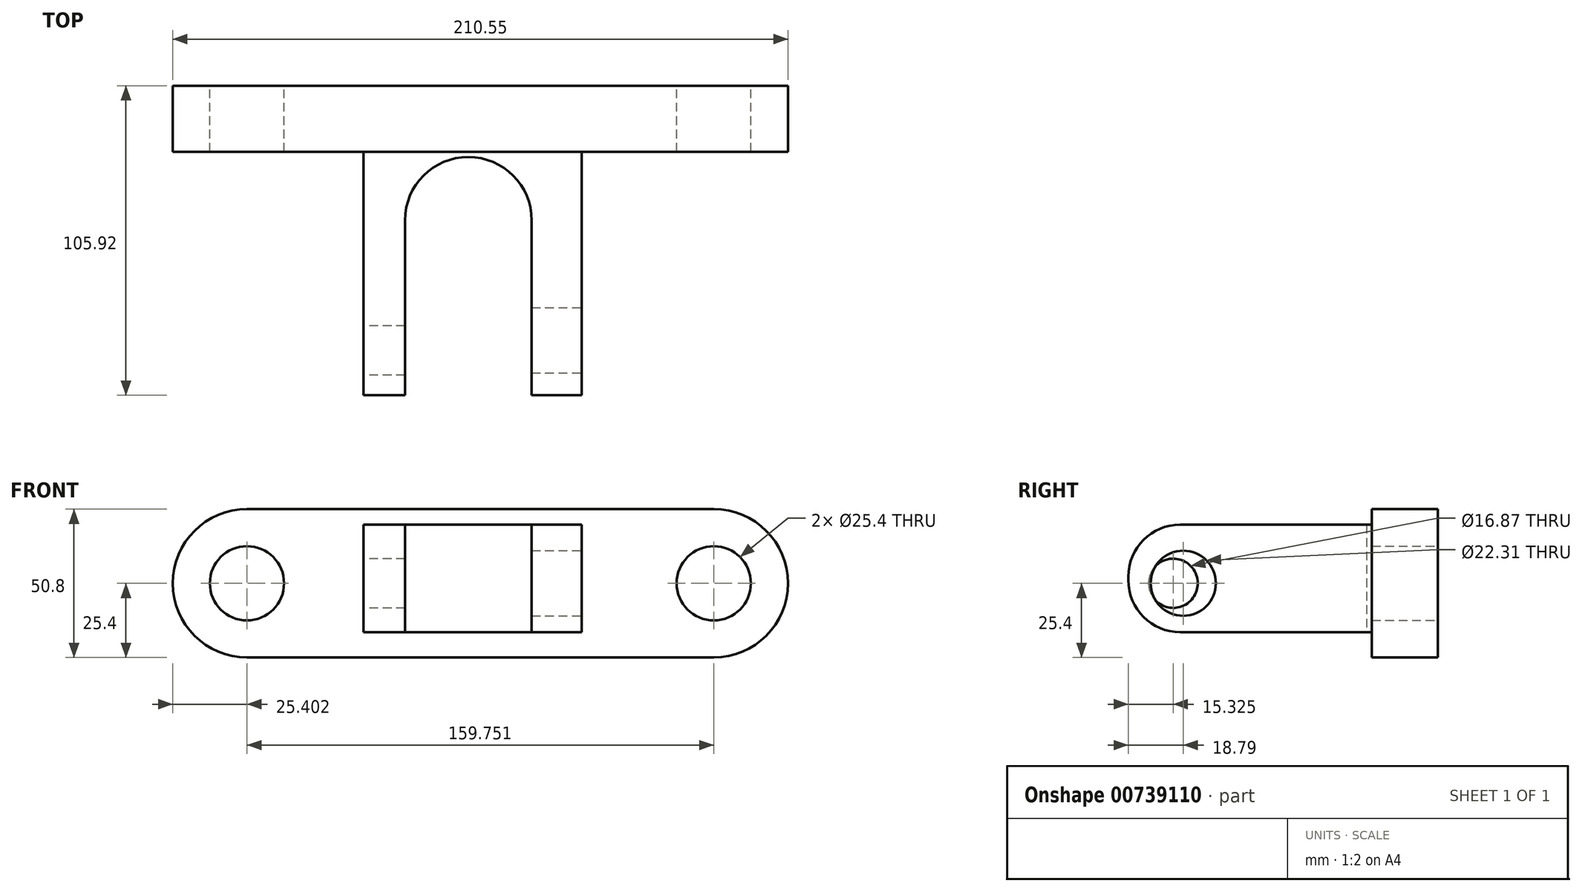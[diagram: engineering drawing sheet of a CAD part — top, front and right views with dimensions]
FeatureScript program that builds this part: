
annotation { "Feature Type Name" : "Feature", "Feature Type Description" : "" }
export const myFeature = defineFeature(function(context is Context, id is Id, definition is map)
    precondition{}
    {
        {
            var Q0;
            Q0=qCreatedBy(makeId("Front.planeOp"),FACE);
            var sketch = newSketch(context, id + "F0", { "sketchPlane" : qUnion([Q0])});
            skArc(sketch, "E0", {"start": v(-77.2, 25.4) * mm, "mid": v(-102.6, 0) * mm, "end": v(-77.2, -25.4) * mm});
            skArc(sketch, "E1", {"start": v(82.55, -25.4) * mm, "mid": v(107.95, 0) * mm, "end": v(82.55, 25.4) * mm});
            skLineSegment(sketch, "E2", {"start": v(-77.2, 25.4) * mm, "end": v(82.55, 25.4) * mm});
            skLineSegment(sketch, "E3", {"start": v(-77.2, -25.4) * mm, "end": v(82.55, -25.4) * mm});
            skCircle(sketch, "E4", {"center": v(-77.2, 0) * mm, "radius": 12.7 * mm});
            skCircle(sketch, "E5", {"center": v(82.55, 0) * mm, "radius": 12.7 * mm});
            skSolve(sketch);
        }
        {
            var Q0;
            Q0 = qSketchRegion(id + "F0", true);
            extrude(context, id + "F1", {"entities" : qUnion([Q0]), "depth" : 22.6 * mm, "offsetDistance" : 25.4 * mm});
        }
        {
            var Q0;
            Q0=makeQuery(id+"F1.opExtrude","CAP_FACE",FACE,{"disambiguationData":[OSD([sQuery(id+"F0.wireOp",EDGE,"E0"),sQuery(id+"F0.wireOp",EDGE,"E1"),sQuery(id+"F0.wireOp",EDGE,"E2"),sQuery(id+"F0.wireOp",EDGE,"E3"),sQuery(id+"F0.wireOp",EDGE,"E4"),sQuery(id+"F0.wireOp",EDGE,"E5")])],"isStart":false});
            var sketch = newSketch(context, id + "F2", { "sketchPlane" : qUnion([Q0])});
            skLineSegment(sketch, "E6.bottom", {"start": v(37.29, -11.17) * mm, "end": v(-37.29, -11.17) * mm});
            skLineSegment(sketch, "E6.top", {"start": v(37.29, 11.17) * mm, "end": v(-37.29, 11.17) * mm});
            skLineSegment(sketch, "E6.left", {"start": v(37.29, -11.17) * mm, "end": v(37.29, 11.17) * mm});
            skLineSegment(sketch, "E6.right", {"start": v(-37.29, -11.17) * mm, "end": v(-37.29, 11.17) * mm});
            skPoint(sketch, "E6.middle", {"position": v(0, 0) * mm});
            skSolve(sketch);
        }
        {
            var Q0;
            Q0=makeQuery(id+"F2.imprint","IMPRINT",FACE,{"disambiguationData":[TD([[makeQuery(id+"F2.imprint","IMPRINT",EDGE,{"derivedFrom":sQuery(id+"F2.wireOp",EDGE,"E6.bottom")}),-1.0]])]});
            extrude(context, id + "F3", {"entities" : qUnion([Q0]), "operationType" : NewBodyOperationType.ADD, "depth" : 83.31 * mm, "offsetDistance" : 25.4 * mm});
        }
        {
            var Q0;
            Q0=makeQuery(id+"F3.opExtrude","SWEPT_FACE",FACE,{"disambiguationData":[OSD([sQuery(id+"F2.wireOp",EDGE,"E6.bottom")])]});
            extrude(context, id + "F4", {"entities" : qUnion([Q0]), "operationType" : NewBodyOperationType.ADD, "depth" : 5.6 * mm, "offsetDistance" : 25.4 * mm});
        }
        {
            var Q0;
            Q0=makeQuery(id+"F3.opExtrude","SWEPT_FACE",FACE,{"disambiguationData":[OSD([sQuery(id+"F2.wireOp",EDGE,"E6.top")])]});
            extrude(context, id + "F5", {"entities" : qUnion([Q0]), "operationType" : NewBodyOperationType.ADD, "depth" : 8.9 * mm, "offsetDistance" : 25.4 * mm});
        }
        {
            var Q0;
            Q0=makeQuery(id+"F4.opExtrude","CAP_FACE",FACE,{"disambiguationData":[OSD([sQuery(id+"F2.wireOp",EDGE,"E6.bottom")])],"isStart":false});
            var sketch = newSketch(context, id + "F6", { "sketchPlane" : qUnion([Q0])});
            skLineSegment(sketch, "E7", {"start": v(-23.11, 105.92) * mm, "end": v(-23.11, 42.42) * mm});
            skLineSegment(sketch, "E8", {"start": v(20.25, 105.92) * mm, "end": v(20.25, 42.42) * mm});
            skArc(sketch, "E9", {"start": v(-23.11, 46.06) * mm, "mid": v(-1.43, 24.38) * mm, "end": v(20.25, 46.06) * mm});
            skLineSegment(sketch, "E10", {"start": v(-23.11, 105.92) * mm, "end": v(20.25, 105.92) * mm});
            skSolve(sketch);
        }
        {
            var Q0;
            Q0 = qSketchRegion(id + "F6", true);
            extrude(context, id + "F7", {"entities" : qUnion([Q0]), "operationType" : NewBodyOperationType.REMOVE, "oppositeDirection" : true, "depth" : 127.25 * mm, "offsetDistance" : 25.4 * mm});
        }
        {
            var Q0;
            {var subQ0=sQuery(id+"F2.wireOp",EDGE,"E6.right");Q0=makeQuery(id+"F5.boolean.opBoolean","MERGE",FACE,{"derivedFrom":[makeQuery(id+"F4.boolean.opBoolean","MERGE",FACE,{"derivedFrom":[makeQuery(id+"F3.opExtrude","SWEPT_FACE",FACE,{"disambiguationData":[OSD([subQ0])]}),makeQuery(id+"F4.opExtrude","SWEPT_FACE",FACE,{"disambiguationData":[OSD([sQuery(id+"F2.wireOp",EDGE,"E6.bottom"),subQ0])]})]}),makeQuery(id+"F5.opExtrude","SWEPT_FACE",FACE,{"disambiguationData":[OSD([sQuery(id+"F2.wireOp",EDGE,"E6.top"),subQ0])]})]});}
            var sketch = newSketch(context, id + "F8", { "sketchPlane" : qUnion([Q0])});
            skCircle(sketch, "E11", {"center": v(90.6, 0) * mm, "radius": 8.44 * mm});
            skSolve(sketch);
        }
        {
            var Q0;
            Q0 = qSketchRegion(id + "F8", true);
            extrude(context, id + "F9", {"entities" : qUnion([Q0]), "operationType" : NewBodyOperationType.REMOVE, "oppositeDirection" : true, "depth" : 25.4 * mm, "offsetDistance" : 25.4 * mm});
        }
        {
            var Q0;
            {var subQ0=sQuery(id+"F2.wireOp",EDGE,"E6.left");Q0=makeQuery(id+"F5.boolean.opBoolean","MERGE",FACE,{"derivedFrom":[makeQuery(id+"F4.boolean.opBoolean","MERGE",FACE,{"derivedFrom":[makeQuery(id+"F3.opExtrude","SWEPT_FACE",FACE,{"disambiguationData":[OSD([subQ0])]}),makeQuery(id+"F4.opExtrude","SWEPT_FACE",FACE,{"disambiguationData":[OSD([sQuery(id+"F2.wireOp",EDGE,"E6.bottom"),subQ0])]})]}),makeQuery(id+"F5.opExtrude","SWEPT_FACE",FACE,{"disambiguationData":[OSD([sQuery(id+"F2.wireOp",EDGE,"E6.top"),subQ0])]})]});}
            var sketch = newSketch(context, id + "F10", { "sketchPlane" : qUnion([Q0])});
            skCircle(sketch, "E12", {"center": v(-87.13, 0) * mm, "radius": 11.16 * mm});
            skSolve(sketch);
        }
        {
            var Q0;
            Q0 = qSketchRegion(id + "F10", true);
            extrude(context, id + "F11", {"entities" : qUnion([Q0]), "operationType" : NewBodyOperationType.REMOVE, "oppositeDirection" : true, "depth" : 25.4 * mm, "offsetDistance" : 25.4 * mm});
        }
        {
            var Q0;
            {var subQ0=sQuery(id+"F2.wireOp",EDGE,"E6.bottom");var subQ1=makeQuery(id+"F3.opExtrude","CAP_EDGE",EDGE,{"disambiguationData":[OSD([subQ0])],"isStart":false});var subQ2=sQuery(id+"F2.wireOp",EDGE,"E6.right");Q0=makeQuery(id+"F7.boolean.opBoolean","SPLIT",EDGE,{"disambiguationData":[TD([makeQuery(id+"F3.opExtrude","SWEPT_FACE",FACE,{"disambiguationData":[OSD([subQ2])]})])],"derivedFrom":makeQuery(id+"F4.opExtrude","CAP_EDGE",EDGE,{"disambiguationData":[OSD([subQ0]),TDD([subQ1])],"isStart":false})});}
            var Q1;
            {var subQ1=sQuery(id+"F2.wireOp",EDGE,"E6.right");var subQ2=sQuery(id+"F2.wireOp",EDGE,"E6.top");var subQ3=makeQuery(id+"F3.opExtrude","CAP_EDGE",EDGE,{"disambiguationData":[OSD([subQ2])],"isStart":false});Q1=makeQuery(id+"F7.boolean.opBoolean","SPLIT",EDGE,{"disambiguationData":[TD([makeQuery(id+"F3.opExtrude","SWEPT_FACE",FACE,{"disambiguationData":[OSD([subQ1])]})])],"derivedFrom":makeQuery(id+"F5.opExtrude","CAP_EDGE",EDGE,{"disambiguationData":[OSD([subQ2]),TDD([subQ3])],"isStart":false})});}
            fillet(context, id + "F12", {"entities" : qUnion([Q0, Q1]), "radius" : 17.78 * mm, "tangentPropagation" : true, "allowEdgeOverflow" : false});
        }
        {
            var Q0;
            {var subQ1=sQuery(id+"F2.wireOp",EDGE,"E6.left");var subQ2=sQuery(id+"F2.wireOp",EDGE,"E6.top");var subQ3=makeQuery(id+"F3.opExtrude","CAP_EDGE",EDGE,{"disambiguationData":[OSD([subQ2])],"isStart":false});Q0=makeQuery(id+"F7.boolean.opBoolean","SPLIT",EDGE,{"disambiguationData":[TD([makeQuery(id+"F3.opExtrude","SWEPT_FACE",FACE,{"disambiguationData":[OSD([subQ1])]})])],"derivedFrom":makeQuery(id+"F5.opExtrude","CAP_EDGE",EDGE,{"disambiguationData":[OSD([subQ2]),TDD([subQ3])],"isStart":false})});}
            var Q1;
            {var subQ0=sQuery(id+"F2.wireOp",EDGE,"E6.bottom");var subQ1=makeQuery(id+"F3.opExtrude","CAP_EDGE",EDGE,{"disambiguationData":[OSD([subQ0])],"isStart":false});var subQ2=sQuery(id+"F2.wireOp",EDGE,"E6.left");Q1=makeQuery(id+"F7.boolean.opBoolean","SPLIT",EDGE,{"disambiguationData":[TD([makeQuery(id+"F3.opExtrude","SWEPT_FACE",FACE,{"disambiguationData":[OSD([subQ2])]})])],"derivedFrom":makeQuery(id+"F4.opExtrude","CAP_EDGE",EDGE,{"disambiguationData":[OSD([subQ0]),TDD([subQ1])],"isStart":false})});}
            fillet(context, id + "F13", {"entities" : qUnion([Q0, Q1]), "radius" : 17.78 * mm, "tangentPropagation" : true, "allowEdgeOverflow" : false});
        }
    });
